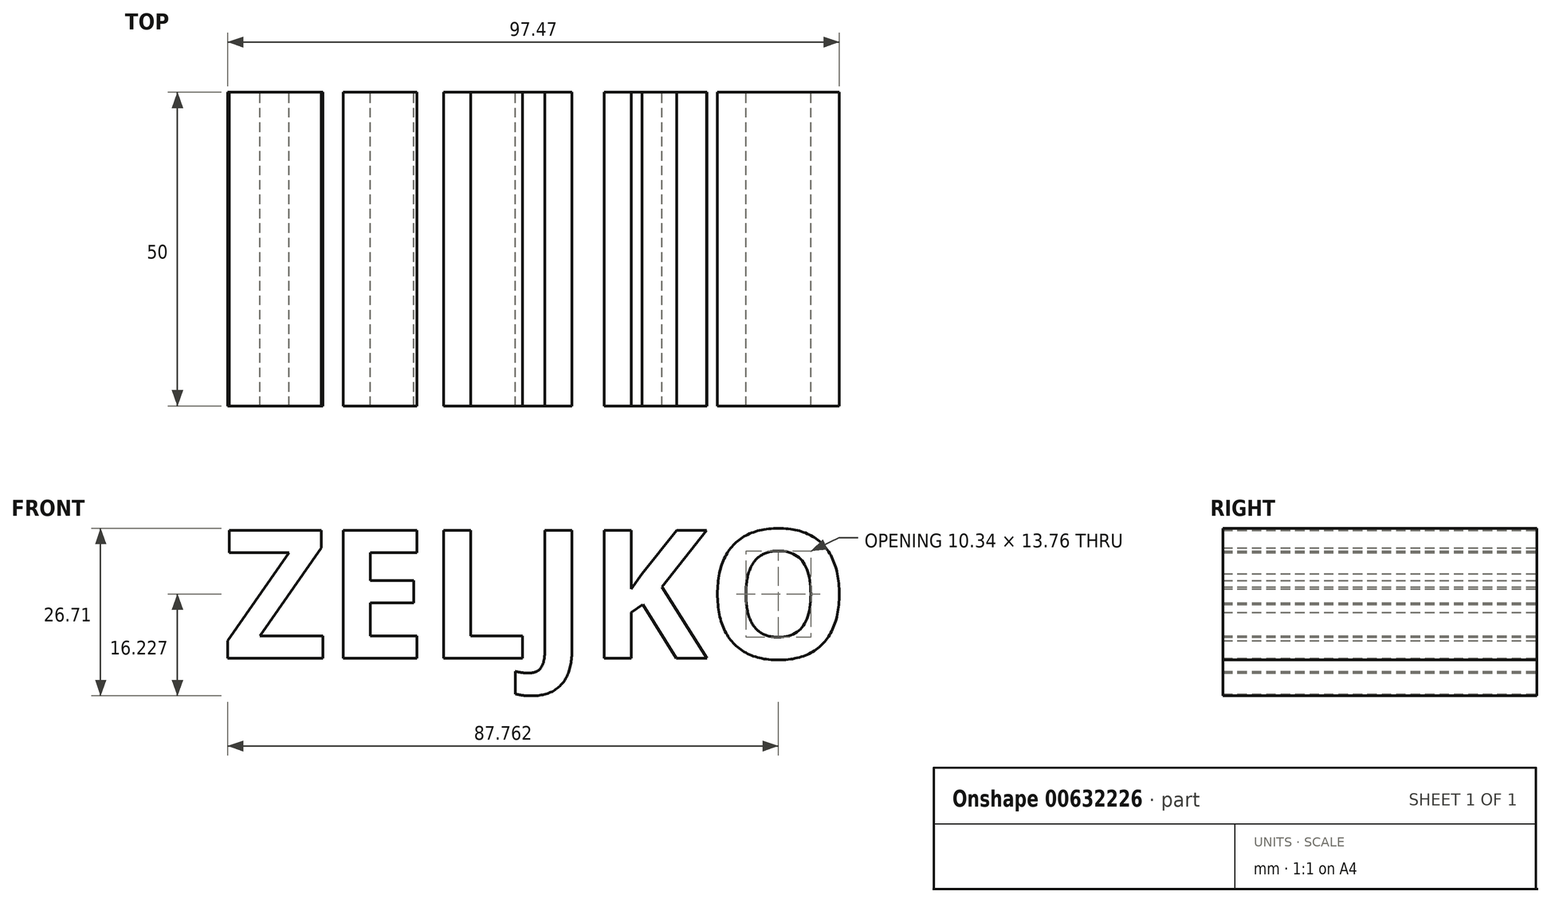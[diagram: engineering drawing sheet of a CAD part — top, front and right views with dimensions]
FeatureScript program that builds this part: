
annotation { "Feature Type Name" : "Feature", "Feature Type Description" : "" }
export const myFeature = defineFeature(function(context is Context, id is Id, definition is map)
    precondition{}
    {
        {
            var Q0;
            Q0=qCreatedBy(makeId("Front.planeOp"),FACE);
            var sketch = newSketch(context, id + "F0", { "sketchPlane" : qUnion([Q0])});
            skText(sketch, "E0", { "text": "ZELJKO", "fontName": "OpenSans-Bold.ttf"});
            const initialGuessF0  = {"E0": [-0.05796, 0.01363, 1, 0, 0.02056]};
            skSetInitialGuess(sketch, initialGuessF0);
            skSolve(sketch);
        }
        {
            var Q0;
            Q0 = qSketchRegion(id + "F0", true);
            extrude(context, id + "F1", {"entities" : qUnion([Q0]), "depth" : 50 * mm, "offsetDistance" : 25 * mm});
        }
    });
